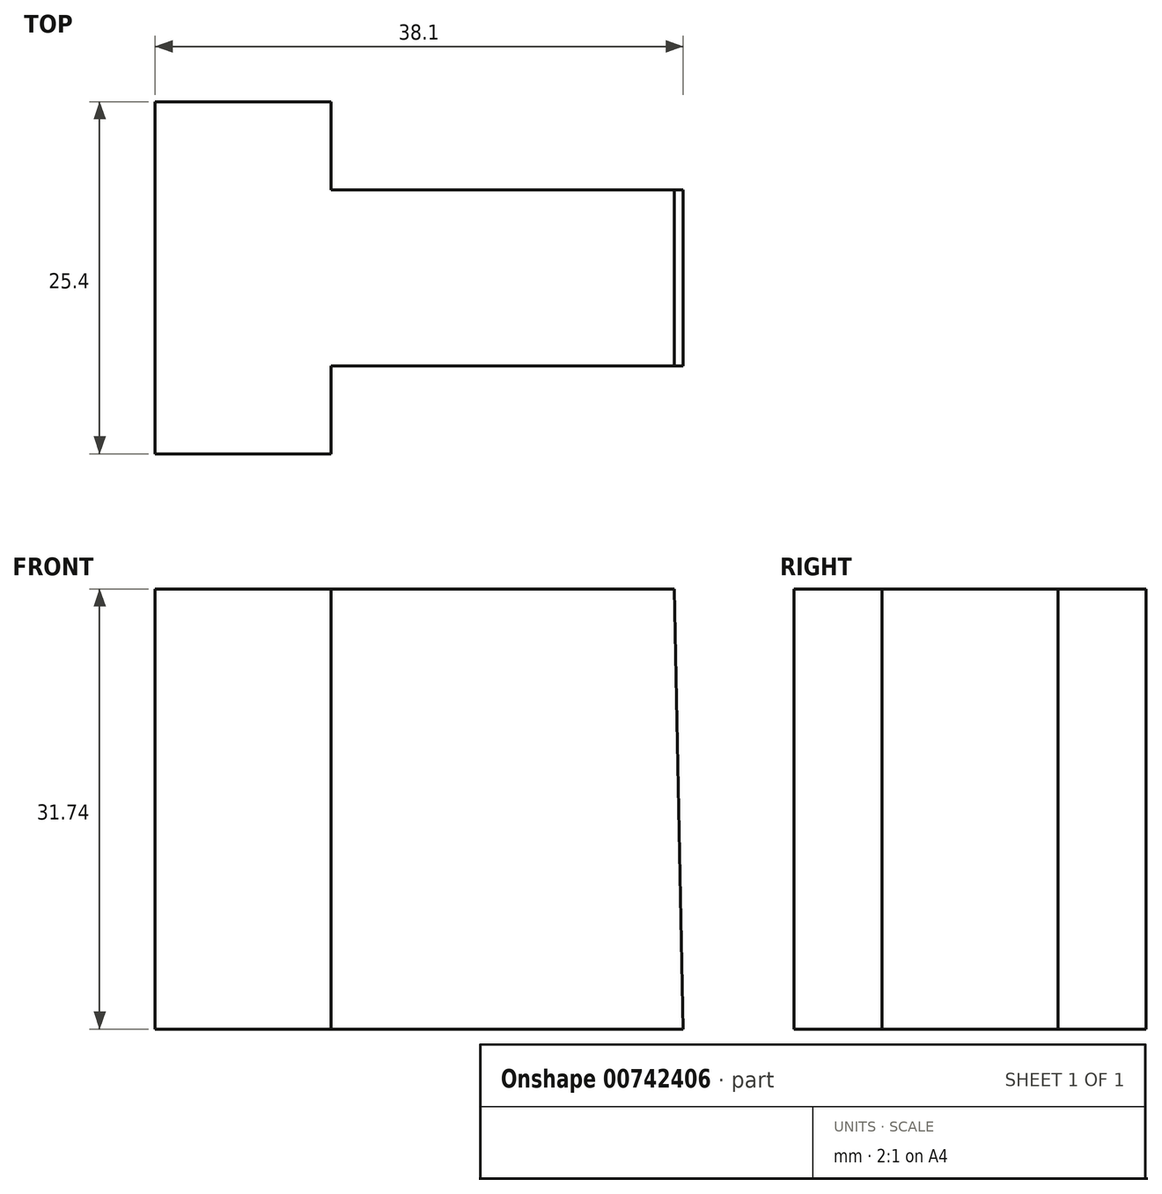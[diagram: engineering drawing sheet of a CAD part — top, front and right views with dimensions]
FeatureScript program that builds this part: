
annotation { "Feature Type Name" : "Feature", "Feature Type Description" : "" }
export const myFeature = defineFeature(function(context is Context, id is Id, definition is map)
    precondition{}
    {
        {
            var Q0;
            Q0=qCreatedBy(makeId("Front.planeOp"),FACE);
            var sketch = newSketch(context, id + "F0", { "sketchPlane" : qUnion([Q0])});
            skLineSegment(sketch, "E0", {"start": v(0, 31.74) * mm, "end": v(0, 0) * mm});
            skLineSegment(sketch, "E1", {"start": v(0, 0) * mm, "end": v(38.1, 0) * mm});
            skLineSegment(sketch, "E2", {"start": v(0, 31.74) * mm, "end": v(37.47, 31.74) * mm});
            skLineSegment(sketch, "E3", {"start": v(37.47, 31.74) * mm, "end": v(38.1, 0) * mm});
            skSolve(sketch);
        }
        {
            var Q0;
            Q0 = qSketchRegion(id + "F0", true);
            extrude(context, id + "F1", {"entities" : qUnion([Q0]), "depth" : 25.4 * mm, "offsetDistance" : 25.4 * mm});
        }
        {
            var Q0;
            Q0=makeQuery(id+"F1.opExtrude","CAP_FACE",FACE,{"disambiguationData":[OSD([sQuery(id+"F0.wireOp",EDGE,"E0"),sQuery(id+"F0.wireOp",EDGE,"E1"),sQuery(id+"F0.wireOp",EDGE,"E2"),sQuery(id+"F0.wireOp",EDGE,"E3")])],"isStart":false});
            var sketch = newSketch(context, id + "F2", { "sketchPlane" : qUnion([Q0])});
            skLineSegment(sketch, "E4", {"start": v(12.7, 31.74) * mm, "end": v(12.7, 0) * mm});
            skSolve(sketch);
        }
        {
            var Q0;
            Q0 = qSketchRegion(id + "F2", true);
            var Q1;
            {var subQ0=sQuery(id+"F2.wireOp",EDGE,"E4");Q1=makeQuery(id+"F2.imprint","IMPRINT",FACE,{"disambiguationData":[TD([[makeQuery(id+"F2.imprint","IMPRINT",EDGE,{"derivedFrom":subQ0}),1.0]])]});}
            extrude(context, id + "F3", {"entities" : qUnion([Q0, Q1]), "operationType" : NewBodyOperationType.REMOVE, "oppositeDirection" : true, "depth" : 6.35 * mm, "offsetDistance" : 25.4 * mm});
        }
        {
            var Q0;
            Q0=makeQuery(id+"F1.opExtrude","CAP_FACE",FACE,{"disambiguationData":[OSD([sQuery(id+"F0.wireOp",EDGE,"E0"),sQuery(id+"F0.wireOp",EDGE,"E1"),sQuery(id+"F0.wireOp",EDGE,"E2"),sQuery(id+"F0.wireOp",EDGE,"E3")])],"isStart":true});
            var sketch = newSketch(context, id + "F4", { "sketchPlane" : qUnion([Q0])});
            skLineSegment(sketch, "E5", {"start": v(-12.7, 0) * mm, "end": v(-12.7, 31.74) * mm});
            skLineSegment(sketch, "E6", {"start": v(-12.7, 31.74) * mm, "end": v(-12.7, 8.53) * mm});
            skSolve(sketch);
        }
        {
            var Q0;
            Q0 = qSketchRegion(id + "F4", true);
            var Q1;
            {var subQ3=sQuery(id+"F4.wireOp",EDGE,"E5");Q1=makeQuery(id+"F4.imprint","IMPRINT",FACE,{"disambiguationData":[TD([[makeQuery(id+"F4.imprint","IMPRINT",EDGE,{"derivedFrom":subQ3}),1.0]])]});}
            extrude(context, id + "F5", {"entities" : qUnion([Q0, Q1]), "operationType" : NewBodyOperationType.REMOVE, "oppositeDirection" : true, "depth" : 6.35 * mm, "offsetDistance" : 25.4 * mm});
        }
    });
